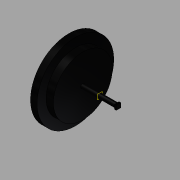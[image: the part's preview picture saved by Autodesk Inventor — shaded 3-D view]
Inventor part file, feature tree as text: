
AUTODESK INVENTOR PART (.ipt)
format: ipt  version: 2015 (Build 190159000, 159)  size: 154,624 bytes
history: native  units: mm
features: extrude x5, sketch x5, fillet x2, plane x1
ambient origin geometry x8: Origin, YZ Plane, XZ Plane, XY Plane, X Axis, Y Axis, Z Axis, Center Point
bodies: Solid1 (feature_tree)
feature tree (13):
  extrude  "Extrusion1"  Depth=12.0mm TaperAngle=0.0deg
  extrude  "Extrusion2"  Depth=19.0mm TaperAngle=0.0deg
  plane  "Work Plane1"
  extrude  "Extrusion6"  Depth=43.0mm
  extrude  "Extrusion9"  Depth=5.0mm TaperAngle=0.0deg
  extrude  "Extrusion10"  Depth=3.0mm TaperAngle=0.0deg
  fillet  "Fillet1"  Radius=2.0mm
  fillet  "Fillet2"  Radius=2.0mm
  sketch  "Sketch2"  dims[d0=33.0mm d1=12.0mm d2=0.0mm]
  sketch  "Sketch3"  dims[d3=2.5mm d4=19.0mm d5=0.0mm]
  sketch  "Sketch7"  dims[d6=-9.5mm d19=43.0mm]
  sketch  "Sketch12"  dims[d20=3.7mm d21=0.0mm d31=5.0mm d32=0.0mm]
  sketch  "Sketch13"  dims[d33=2.0mm d34=3.0mm d35=0.0mm d36=2.0mm d37=2.0mm]
